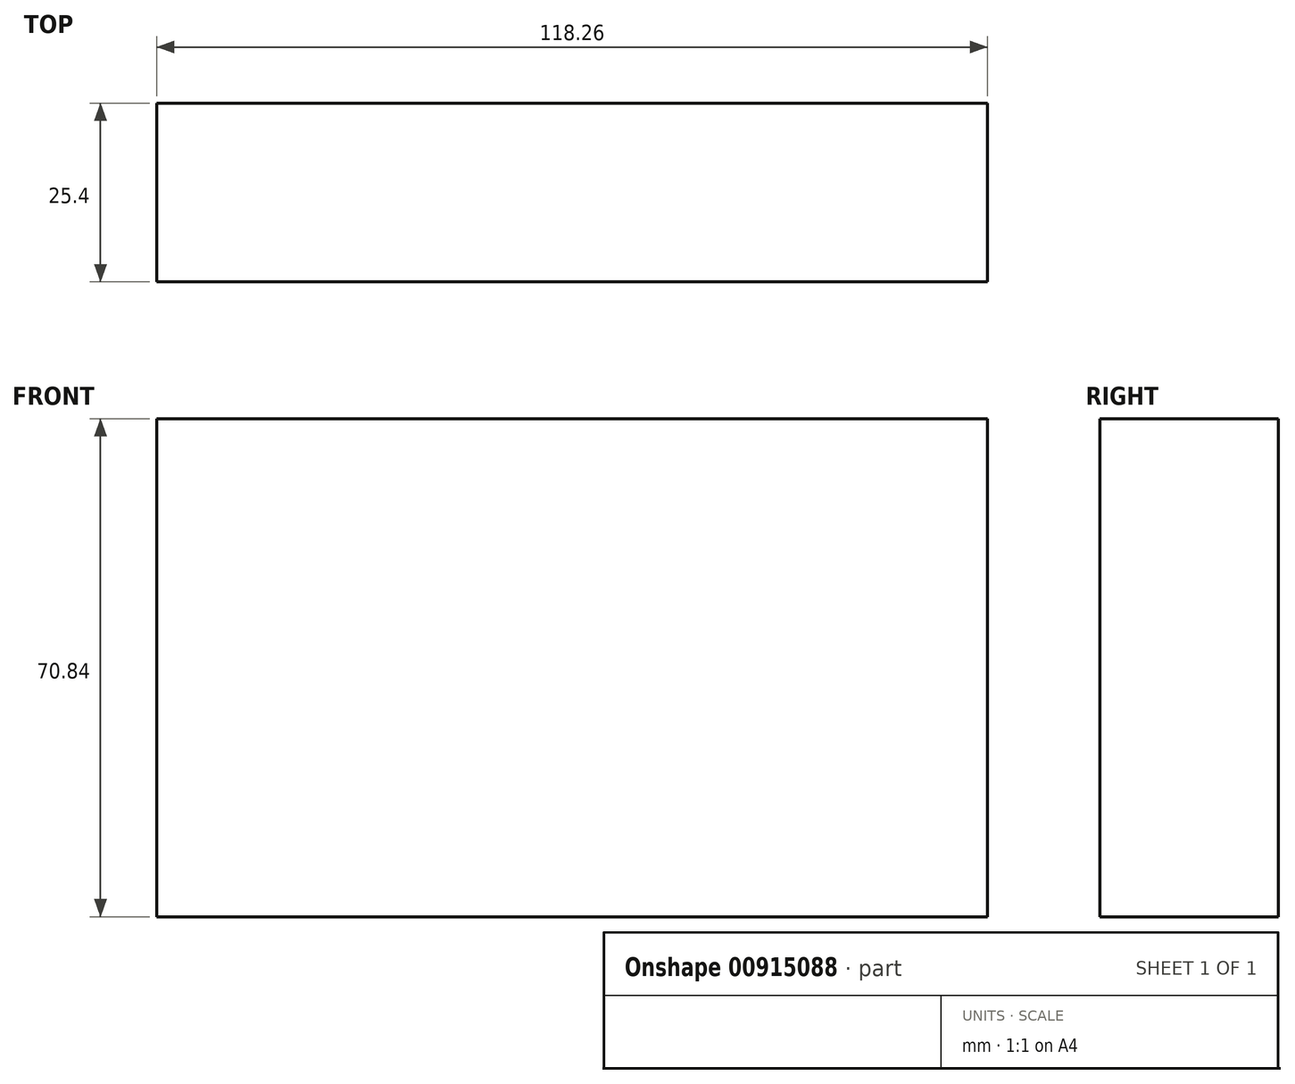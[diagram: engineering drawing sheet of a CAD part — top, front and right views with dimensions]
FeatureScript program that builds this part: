
annotation { "Feature Type Name" : "Feature", "Feature Type Description" : "" }
export const myFeature = defineFeature(function(context is Context, id is Id, definition is map)
    precondition{}
    {
        {
            var Q0;
            Q0=qCreatedBy(makeId("Front.planeOp"),FACE);
            var sketch = newSketch(context, id + "F0", { "sketchPlane" : qUnion([Q0])});
            skLineSegment(sketch, "E0.bottom", {"start": v(-57.72, 33.04) * mm, "end": v(60.54, 33.04) * mm});
            skLineSegment(sketch, "E0.top", {"start": v(-57.72, -37.8) * mm, "end": v(60.54, -37.8) * mm});
            skLineSegment(sketch, "E0.left", {"start": v(-57.72, 33.04) * mm, "end": v(-57.72, -37.8) * mm});
            skLineSegment(sketch, "E0.right", {"start": v(60.54, 33.04) * mm, "end": v(60.54, -37.8) * mm});
            skSolve(sketch);
        }
        {
            var Q0;
            Q0 = qSketchRegion(id + "F0", true);
            extrude(context, id + "F1", {"entities" : qUnion([Q0]), "depth" : 25.4 * mm, "offsetDistance" : 25.4 * mm});
        }
    });
